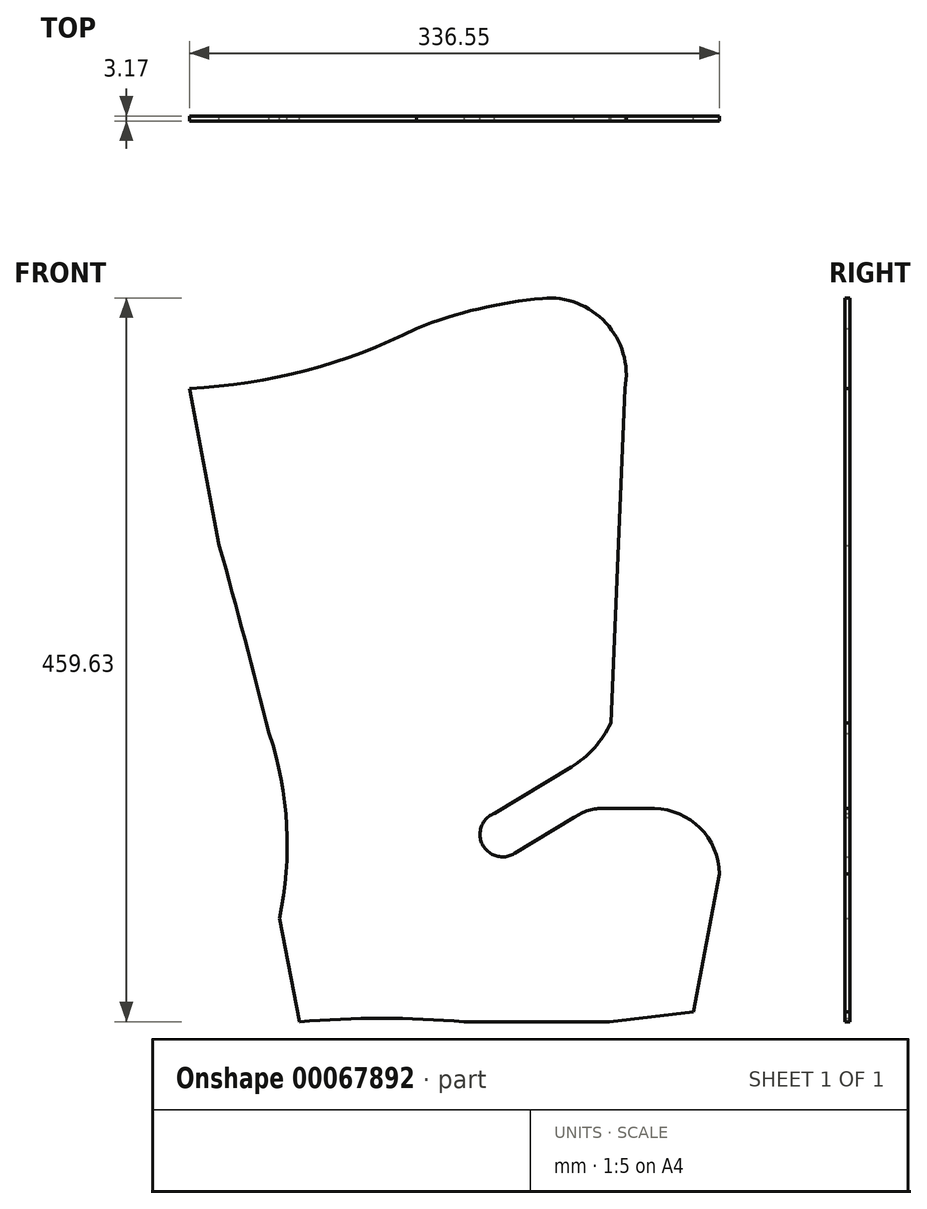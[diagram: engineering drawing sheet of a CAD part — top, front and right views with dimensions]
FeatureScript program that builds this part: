
annotation { "Feature Type Name" : "Feature", "Feature Type Description" : "" }
export const myFeature = defineFeature(function(context is Context, id is Id, definition is map)
    precondition{}
    {
        {
            var Q0;
            Q0=qCreatedBy(makeId("Front.planeOp"),FACE);
            var sketch = newSketch(context, id + "F0", { "sketchPlane" : qUnion([Q0])});
            skArc(sketch, "E0", {"start": v(104.78, 0) * mm, "mid": v(52.39, 2.12) * mm, "end": v(0, 0) * mm});
            skLineSegment(sketch, "E1", {"start": v(104.78, 0) * mm, "end": v(196.85, 0) * mm});
            skLineSegment(sketch, "E2", {"start": v(196.85, 0) * mm, "end": v(250.45, 6.35) * mm});
            skLineSegment(sketch, "E3", {"start": v(0, 0) * mm, "end": v(-12.7, 65.45) * mm});
            skLineSegment(sketch, "E4", {"start": v(250.45, 6.35) * mm, "end": v(266.7, 93.75) * mm});
            skArc(sketch, "E5", {"start": v(-12.7, 65.45) * mm, "mid": v(-7.96, 124.62) * mm, "end": v(-19.05, 182.93) * mm});
            skLineSegment(sketch, "E6", {"start": v(-50.8, 302.48) * mm, "end": v(-69.85, 402.28) * mm});
            skArc(sketch, "E7", {"start": v(-69.85, 402.28) * mm, "mid": v(4.31, 413.68) * mm, "end": v(74.43, 440.38) * mm});
            skArc(sketch, "E8", {"start": v(206.9, 402.28) * mm, "mid": v(194.82, 443.84) * mm, "end": v(154.45, 459.43) * mm});
            skArc(sketch, "E9", {"start": v(266.7, 93.75) * mm, "mid": v(254.6, 123.02) * mm, "end": v(225.43, 135.3) * mm});
            skLineSegment(sketch, "E10", {"start": v(225.43, 135.3) * mm, "end": v(193.68, 135.57) * mm});
            skArc(sketch, "E11", {"start": v(193.68, 135.57) * mm, "mid": v(183.68, 134.1) * mm, "end": v(174.6, 129.68) * mm});
            skLineSegment(sketch, "E12", {"start": v(174.6, 129.68) * mm, "end": v(136.53, 106.73) * mm});
            skArc(sketch, "E13", {"start": v(123.82, 132.33) * mm, "mid": v(116.28, 112.63) * mm, "end": v(136.53, 106.73) * mm});
            skLineSegment(sketch, "E14", {"start": v(172.77, 161.83) * mm, "end": v(123.82, 132.33) * mm});
            skLineSegment(sketch, "E15", {"start": v(206.9, 402.28) * mm, "end": v(197.81, 189.75) * mm});
            skArc(sketch, "E16", {"start": v(172.77, 161.83) * mm, "mid": v(187.38, 173.92) * mm, "end": v(197.81, 189.75) * mm});
            skArc(sketch, "E17", {"start": v(154.45, 459.43) * mm, "mid": v(113.76, 452.76) * mm, "end": v(74.43, 440.38) * mm});
            skArc(sketch, "E18", {"start": v(-19.05, 182.93) * mm, "mid": v(-34.53, 242.8) * mm, "end": v(-50.8, 302.48) * mm});
            skSolve(sketch);
        }
        {
            var Q0;
            Q0=makeQuery(id+"F0.imprint","IMPRINT",FACE,{"disambiguationData":[TD([[makeQuery(id+"F0.imprint","IMPRINT",EDGE,{"derivedFrom":sQuery(id+"F0.wireOp",EDGE,"E0")}),-1.0]])]});
            extrude(context, id + "F1", {"entities" : qUnion([Q0]), "depth" : 3.17 * mm});
        }
    });
